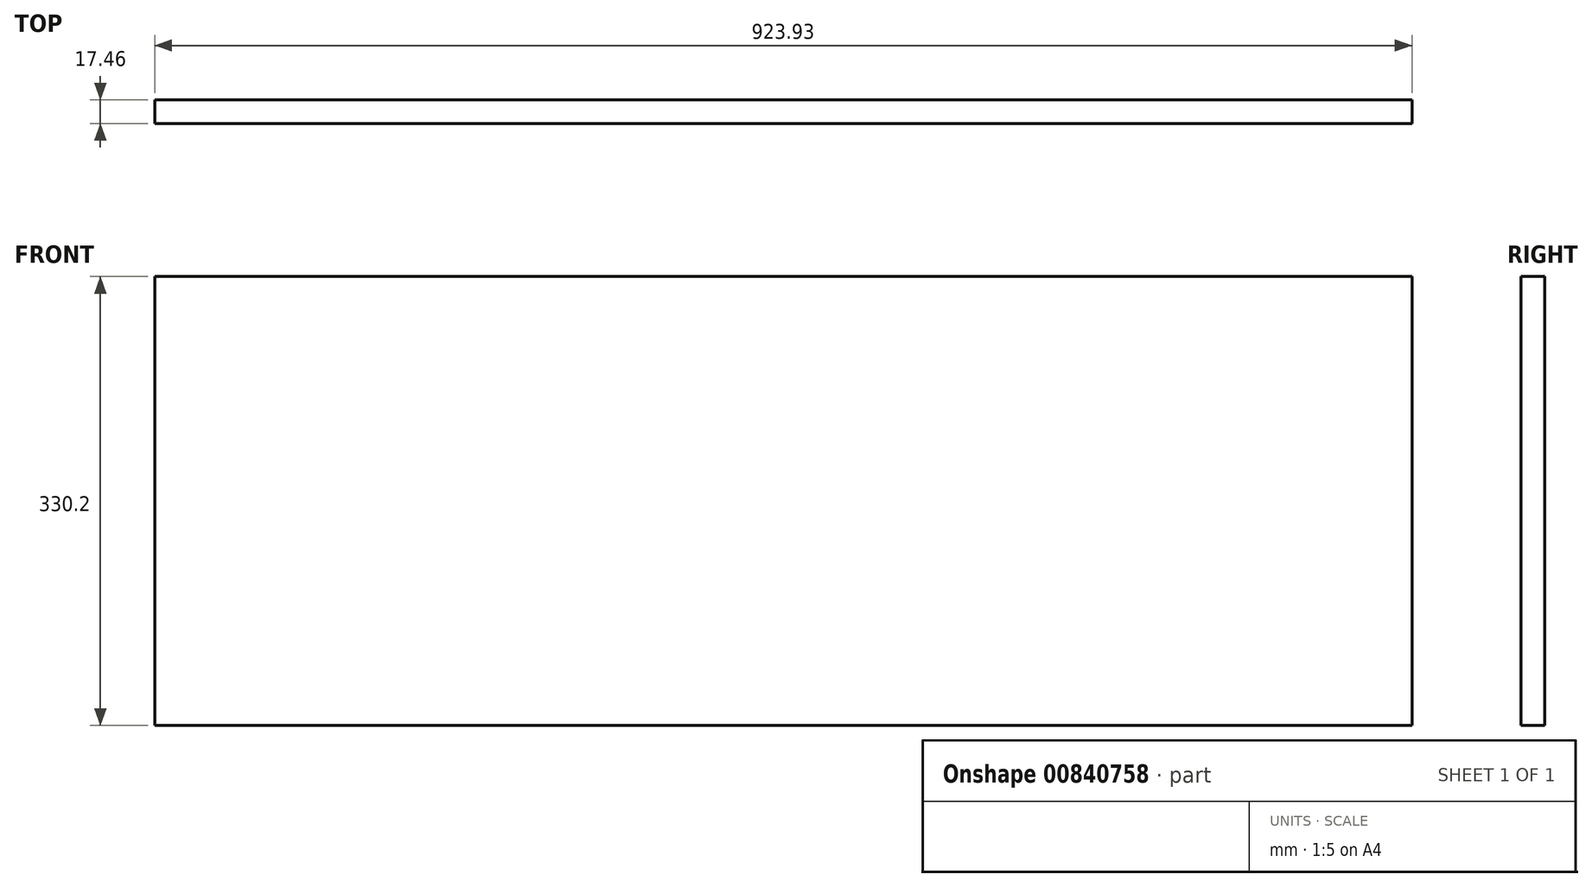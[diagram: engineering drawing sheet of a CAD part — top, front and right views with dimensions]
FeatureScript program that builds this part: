
annotation { "Feature Type Name" : "Feature", "Feature Type Description" : "" }
export const myFeature = defineFeature(function(context is Context, id is Id, definition is map)
    precondition{}
    {
        {
            var Q0;
            Q0=qCreatedBy(makeId("Front.planeOp"),FACE);
            var sketch = newSketch(context, id + "F0", { "sketchPlane" : qUnion([Q0])});
            skLineSegment(sketch, "E0.bottom", {"start": v(-467.68, 33.2) * mm, "end": v(456.25, 33.2) * mm});
            skLineSegment(sketch, "E0.top", {"start": v(-467.68, -297) * mm, "end": v(456.25, -297) * mm});
            skLineSegment(sketch, "E0.left", {"start": v(-467.68, 33.2) * mm, "end": v(-467.68, -297) * mm});
            skLineSegment(sketch, "E0.right", {"start": v(456.25, 33.2) * mm, "end": v(456.25, -297) * mm});
            skSolve(sketch);
        }
        {
            var Q0;
            Q0=makeQuery(id+"F0.imprint","IMPRINT",FACE,{"disambiguationData":[TD([[makeQuery(id+"F0.imprint","IMPRINT",EDGE,{"derivedFrom":sQuery(id+"F0.wireOp",EDGE,"E0.bottom")}),-1.0]])]});
            extrude(context, id + "F1", {"entities" : qUnion([Q0]), "depth" : 17.46 * mm, "offsetDistance" : 25.4 * mm});
        }
    });
